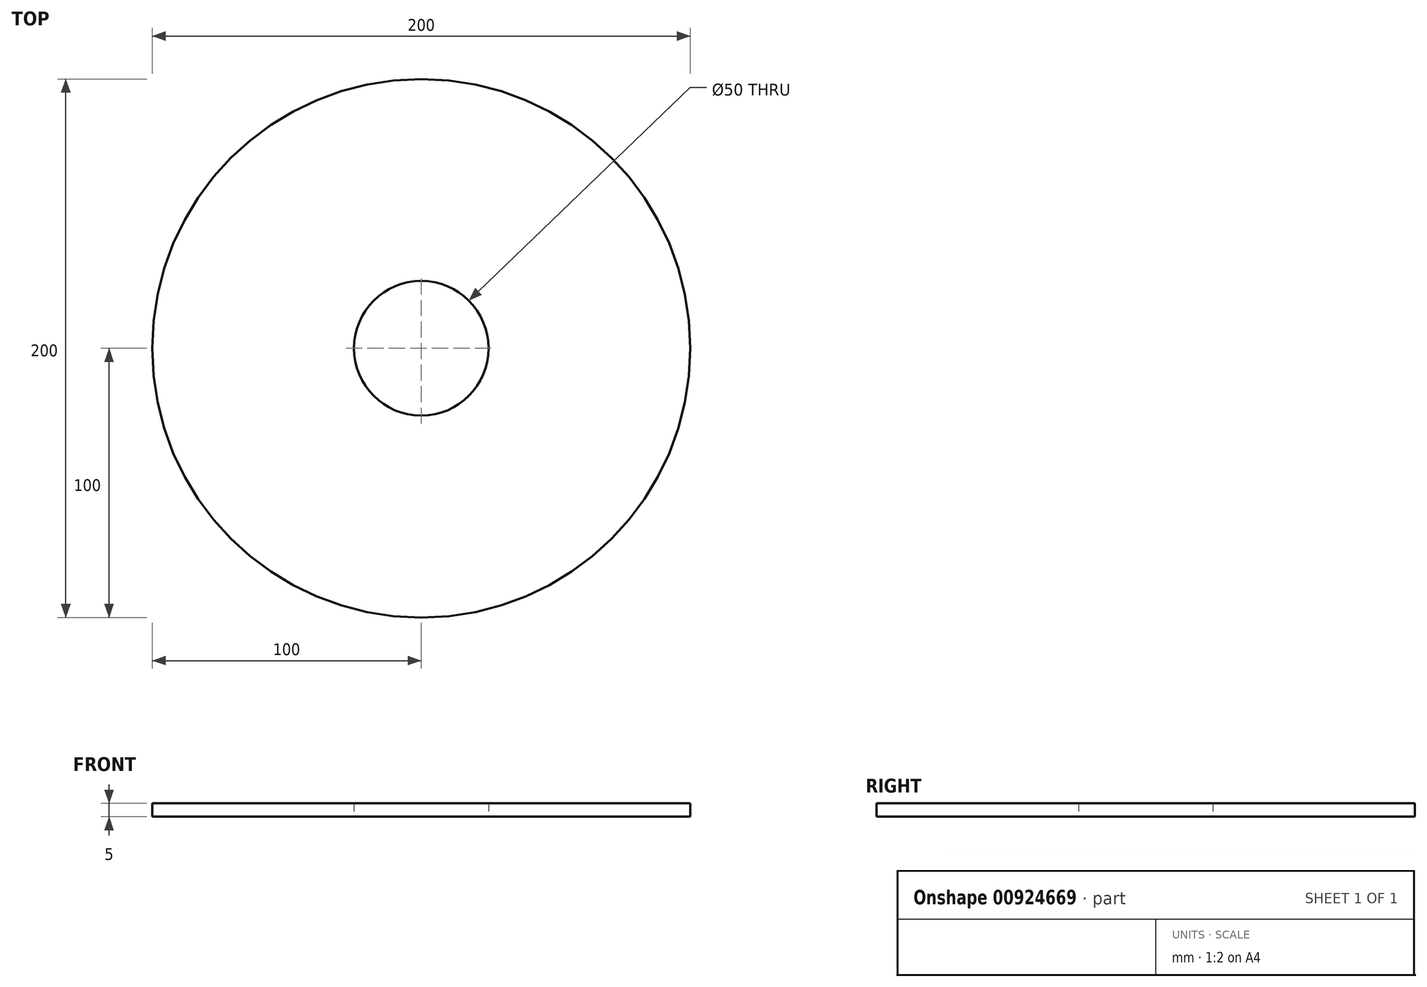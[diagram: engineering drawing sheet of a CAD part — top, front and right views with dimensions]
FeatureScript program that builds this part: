
annotation { "Feature Type Name" : "Feature", "Feature Type Description" : "" }
export const myFeature = defineFeature(function(context is Context, id is Id, definition is map)
    precondition{}
    {
        {
            var Q0;
            Q0=qCreatedBy(makeId("Top.planeOp"),FACE);
            var sketch = newSketch(context, id + "F0", { "sketchPlane" : qUnion([Q0])});
            skCircle(sketch, "E0", {"center": v(0, 0) * mm, "radius": 25 * mm});
            skCircle(sketch, "E1", {"center": v(0, 0) * mm, "radius": 100 * mm});
            skSolve(sketch);
        }
        {
            var Q0;
            Q0=makeQuery(id+"F0.imprint","IMPRINT",FACE,{"disambiguationData":[TD([[makeQuery(id+"F0.imprint","IMPRINT",EDGE,{"derivedFrom":sQuery(id+"F0.wireOp",EDGE,"E0")}),-1.0]])]});
            extrude(context, id + "F1", {"entities" : qUnion([Q0]), "depth" : 5 * mm, "offsetDistance" : 25 * mm});
        }
    });
